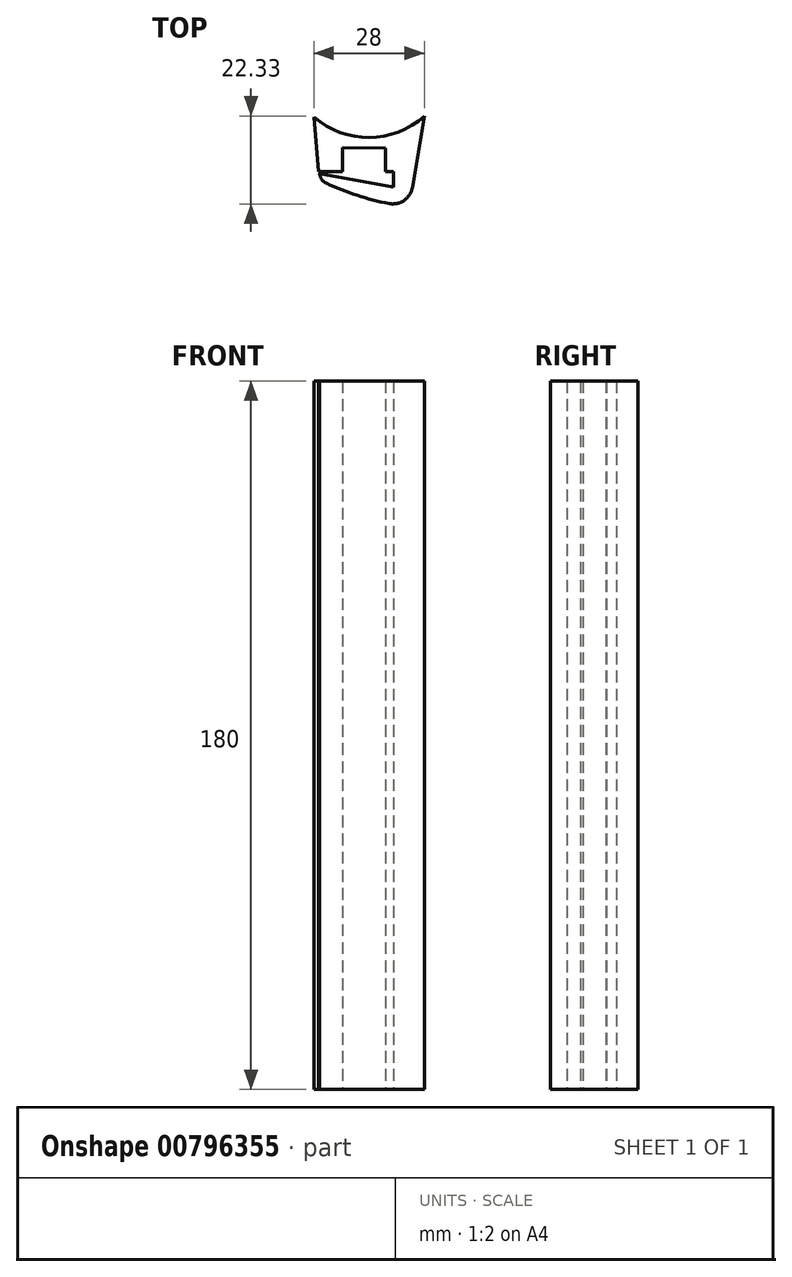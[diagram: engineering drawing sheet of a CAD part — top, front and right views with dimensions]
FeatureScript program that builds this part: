
annotation { "Feature Type Name" : "Feature", "Feature Type Description" : "" }
export const myFeature = defineFeature(function(context is Context, id is Id, definition is map)
    precondition{}
    {
        {
            var Q0;
            Q0=qCreatedBy(makeId("Top.planeOp"),FACE);
            var sketch = newSketch(context, id + "F0", { "sketchPlane" : qUnion([Q0])});
            skArc(sketch, "E0", {"start": v(-13.88, -15.76) * mm, "mid": v(0.16, -21) * mm, "end": v(14.12, -15.54) * mm});
            skLineSegment(sketch, "E1", {"start": v(-13.88, -15.76) * mm, "end": v(-12.71, -29.61) * mm});
            skLineSegment(sketch, "E2", {"start": v(14.12, -15.54) * mm, "end": v(10.28, -38.54) * mm});
            skLineSegment(sketch, "E3", {"start": v(-12.47, -31.79) * mm, "end": v(-12.47, -30.21) * mm});
            skLineSegment(sketch, "E4", {"start": v(-12.47, -30.21) * mm, "end": v(6.28, -33.61) * mm});
            skLineSegment(sketch, "E5", {"start": v(6.28, -33.61) * mm, "end": v(6.29, -29.61) * mm});
            skLineSegment(sketch, "E6", {"start": v(6.29, -29.61) * mm, "end": v(4.29, -29.6) * mm});
            skLineSegment(sketch, "E7", {"start": v(4.29, -29.6) * mm, "end": v(4.29, -23.66) * mm});
            skLineSegment(sketch, "E8", {"start": v(4.29, -23.66) * mm, "end": v(-6.71, -23.6) * mm});
            skLineSegment(sketch, "E9", {"start": v(-6.71, -23.6) * mm, "end": v(-6.71, -29.6) * mm});
            skLineSegment(sketch, "E10", {"start": v(-6.71, -29.6) * mm, "end": v(-12.71, -29.61) * mm});
            skArc(sketch, "E11", {"start": v(-12.47, -31.79) * mm, "mid": v(-1.4, -36.17) * mm, "end": v(10.28, -38.54) * mm});
            skSolve(sketch);
        }
        {
            var Q0;
            Q0 = qSketchRegion(id + "F0", true);
            extrude(context, id + "F1", {"entities" : qUnion([Q0]), "depth" : 180 * mm, "offsetDistance" : 25 * mm});
        }
        {
            var Q0;
            Q0=makeQuery(id+"F1.opExtrude","SWEPT_EDGE",EDGE,{"disambiguationData":[OSD([sQuery(id+"F0.wireOp",EDGE,"E2"),sQuery(id+"F0.wireOp",EDGE,"E11")])]});
            fillet(context, id + "F2", {"entities" : qUnion([Q0]), "radius" : 5 * mm, "tangentPropagation" : true, "allowEdgeOverflow" : false});
        }
        {
            var Q0;
            Q0=makeQuery(id+"F1.opExtrude","SWEPT_EDGE",EDGE,{"disambiguationData":[OSD([sQuery(id+"F0.wireOp",EDGE,"E3"),sQuery(id+"F0.wireOp",EDGE,"E11")])]});
            fillet(context, id + "F3", {"entities" : qUnion([Q0]), "radius" : 3 * mm, "tangentPropagation" : true, "allowEdgeOverflow" : false});
        }
    });
